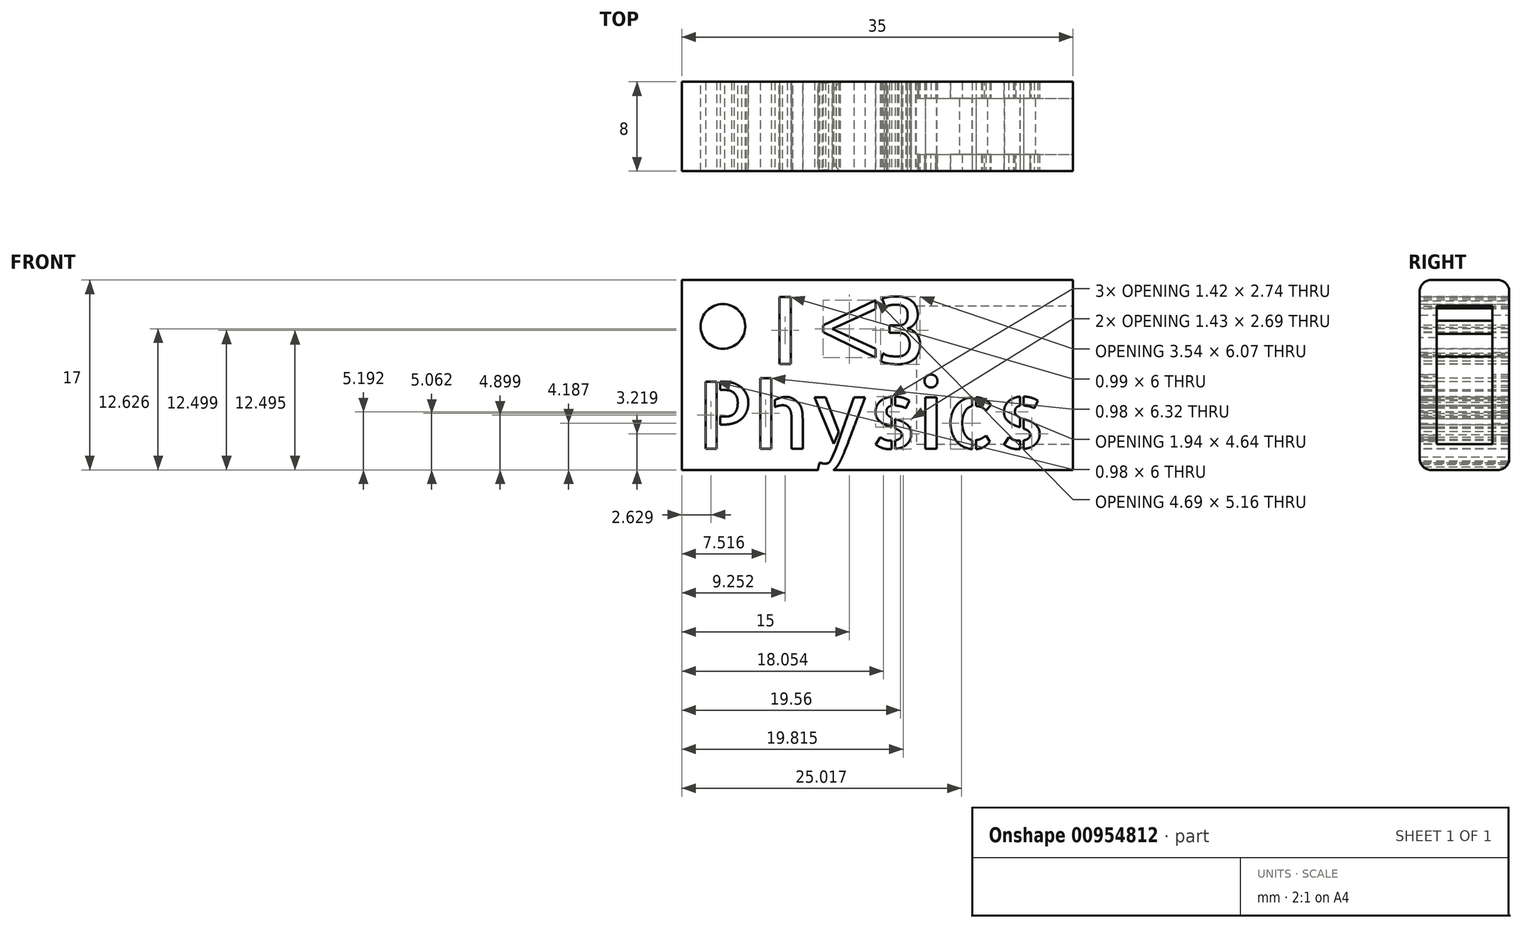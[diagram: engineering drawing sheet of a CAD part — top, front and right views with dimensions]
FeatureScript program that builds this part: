
annotation { "Feature Type Name" : "Feature", "Feature Type Description" : "" }
export const myFeature = defineFeature(function(context is Context, id is Id, definition is map)
    precondition{}
    {
        {
            var Q0;
            Q0=qCreatedBy(makeId("Top.planeOp"),FACE);
            var sketch = newSketch(context, id + "F0", { "sketchPlane" : qUnion([Q0])});
            skLineSegment(sketch, "E0.bottom", {"start": v(-7.5, 4) * mm, "end": v(7.5, 4) * mm});
            skLineSegment(sketch, "E0.top", {"start": v(-7.5, -4) * mm, "end": v(7.5, -4) * mm});
            skLineSegment(sketch, "E0.left", {"start": v(-8.5, 3) * mm, "end": v(-8.5, -3) * mm});
            skLineSegment(sketch, "E0.right", {"start": v(8.5, 3) * mm, "end": v(8.5, -3) * mm});
            skPoint(sketch, "E0.middle", {"position": v(0, 0) * mm});
            skPoint(sketch, "E1.visualSharp", {"position": v(-8.5, 4) * mm});
            skArc(sketch, "E1.filletArc", {"start": v(-7.5, 4) * mm, "mid": v(-8.2, 3.7) * mm, "end": v(-8.5, 3) * mm});
            skPoint(sketch, "E2.visualSharp", {"position": v(8.5, 4) * mm});
            skArc(sketch, "E2.filletArc", {"start": v(8.5, 3) * mm, "mid": v(8.2, 3.7) * mm, "end": v(7.5, 4) * mm});
            skPoint(sketch, "E3.visualSharp", {"position": v(8.5, -4) * mm});
            skArc(sketch, "E3.filletArc", {"start": v(7.5, -4) * mm, "mid": v(8.2, -3.7) * mm, "end": v(8.5, -3) * mm});
            skPoint(sketch, "E4.visualSharp", {"position": v(-8.5, -4) * mm});
            skArc(sketch, "E4.filletArc", {"start": v(-8.5, -3) * mm, "mid": v(-8.2, -3.7) * mm, "end": v(-7.5, -4) * mm});
            skSolve(sketch);
        }
        {
            var Q0;
            Q0=qSketchRegion(id+"F0",true);
            extrude(context, id + "F1", {"entities" : qUnion([Q0]), "depth" : 35 * mm, "offsetDistance" : 25 * mm});
        }
        {
            var Q0;
            Q0=makeQuery(id+"F1.opExtrude","CAP_FACE",FACE,{"disambiguationData":[OSD([sQuery(id+"F0.wireOp",EDGE,"E0.bottom"),sQuery(id+"F0.wireOp",EDGE,"E0.top"),sQuery(id+"F0.wireOp",EDGE,"E0.left"),sQuery(id+"F0.wireOp",EDGE,"E0.right"),sQuery(id+"F0.wireOp",EDGE,"E1.filletArc"),sQuery(id+"F0.wireOp",EDGE,"E2.filletArc"),sQuery(id+"F0.wireOp",EDGE,"E3.filletArc"),sQuery(id+"F0.wireOp",EDGE,"E4.filletArc")])],"isStart":true});
            var sketch = newSketch(context, id + "F2", { "sketchPlane" : qUnion([Q0])});
            skLineSegment(sketch, "E5.bottom", {"start": v(6.2, 2.5) * mm, "end": v(-6.2, 2.5) * mm});
            skLineSegment(sketch, "E5.top", {"start": v(6.2, -2.5) * mm, "end": v(-6.2, -2.5) * mm});
            skLineSegment(sketch, "E5.left", {"start": v(6.2, 2.5) * mm, "end": v(6.2, -2.5) * mm});
            skLineSegment(sketch, "E5.right", {"start": v(-6.2, 2.5) * mm, "end": v(-6.2, -2.5) * mm});
            skPoint(sketch, "E5.middle", {"position": v(0, 0) * mm});
            skSolve(sketch);
        }
        {
            var Q0;
            Q0=qSketchRegion(id+"F2",true);
            extrude(context, id + "F3", {"entities" : qUnion([Q0]), "operationType" : NewBodyOperationType.REMOVE, "oppositeDirection" : true, "depth" : 14 * mm, "offsetDistance" : 25 * mm});
        }
        {
            var Q0;
            Q0=makeQuery(id+"F1.opExtrude","SWEPT_BODY",BODY,{"disambiguationData":[OSD([sQuery(id+"F0.wireOp",EDGE,"E0.bottom"),sQuery(id+"F0.wireOp",EDGE,"E0.top"),sQuery(id+"F0.wireOp",EDGE,"E0.left"),sQuery(id+"F0.wireOp",EDGE,"E0.right"),sQuery(id+"F0.wireOp",EDGE,"E1.filletArc"),sQuery(id+"F0.wireOp",EDGE,"E2.filletArc"),sQuery(id+"F0.wireOp",EDGE,"E3.filletArc"),sQuery(id+"F0.wireOp",EDGE,"E4.filletArc")])]});
            var Q1;
            Q1=makeQuery(id+"F1.opExtrude","CAP_EDGE",EDGE,{"disambiguationData":[OSD([sQuery(id+"F0.wireOp",EDGE,"E0.right")])],"isStart":true});
            transform(context, id + "F4", {"entities" : qUnion([Q0]), "transformType" : TransformType.ROTATION, "transformAxis" : qUnion([Q1]), "angle" : 90 * degree, "makeCopy" : false});
        }
        {
            var Q0;
            Q0=makeQuery(id+"F1.opExtrude","SWEPT_FACE",FACE,{"disambiguationData":[OSD([sQuery(id+"F0.wireOp",EDGE,"E0.top")])]});
            var sketch = newSketch(context, id + "F5", { "sketchPlane" : qUnion([Q0])});
            skText(sketch, "E6", { "text": "I   3", "fontName": "AllertaStencil-Regular.ttf"});
            const initialGuessF5  = {"E6": [-0.01851, -0.0075, 1, 0, 0.006]};
            skSetInitialGuess(sketch, initialGuessF5);
            skSolve(sketch);
        }
        {
            var Q0;
            Q0=qSketchRegion(id+"F5",true);
            extrude(context, id + "F6", {"entities" : qUnion([Q0]), "operationType" : NewBodyOperationType.REMOVE, "oppositeDirection" : true, "depth" : 8 * mm, "offsetDistance" : 25 * mm});
        }
        {
            var Q0;
            Q0=makeQuery(id+"F1.opExtrude","SWEPT_FACE",FACE,{"disambiguationData":[OSD([sQuery(id+"F0.wireOp",EDGE,"E0.bottom")])]});
            var sketch = newSketch(context, id + "F7", { "sketchPlane" : qUnion([Q0])});
            skCircle(sketch, "E7", {"center": v(22.81, -4.15) * mm, "radius": 2 * mm});
            skSolve(sketch);
        }
        {
            var Q0;
            Q0=qSketchRegion(id+"F7",true);
            extrude(context, id + "F8", {"entities" : qUnion([Q0]), "operationType" : NewBodyOperationType.REMOVE, "oppositeDirection" : true, "depth" : 8 * mm, "offsetDistance" : 25 * mm});
        }
        {
            var Q0;
            Q0=makeQuery(id+"F1.opExtrude","SWEPT_FACE",FACE,{"disambiguationData":[OSD([sQuery(id+"F0.wireOp",EDGE,"E0.top")])]});
            var sketch = newSketch(context, id + "F9", { "sketchPlane" : qUnion([Q0])});
            skText(sketch, "E8", { "text": "Physics", "fontName": "AllertaStencil-Regular.ttf"});
            const initialGuessF9  = {"E8": [-0.0251, -0.0151, 1, 0, 0.006]};
            skSetInitialGuess(sketch, initialGuessF9);
            skSolve(sketch);
        }
        {
            var Q0;
            Q0=qSketchRegion(id+"F9",true);
            extrude(context, id + "F10", {"entities" : qUnion([Q0]), "operationType" : NewBodyOperationType.REMOVE, "oppositeDirection" : true, "depth" : 8 * mm, "offsetDistance" : 25 * mm});
        }
        {
            var Q0;
            Q0=makeQuery(id+"F1.opExtrude","SWEPT_FACE",FACE,{"disambiguationData":[OSD([sQuery(id+"F0.wireOp",EDGE,"E0.top")])]});
            var sketch = newSketch(context, id + "F11", { "sketchPlane" : qUnion([Q0])});
            skText(sketch, "E9", { "text": "<", "fontName": "AllertaStencil-Regular.ttf"});
            const initialGuessF11  = {"E9": [-0.0141, -0.0069, 1, 0, 0.0065]};
            skSetInitialGuess(sketch, initialGuessF11);
            skSolve(sketch);
        }
        {
            var Q0;
            Q0 = qSketchRegion(id + "F11", true);
            extrude(context, id + "F12", {"entities" : qUnion([Q0]), "operationType" : NewBodyOperationType.REMOVE, "oppositeDirection" : true, "depth" : 8 * mm, "offsetDistance" : 25 * mm});
        }
    });
